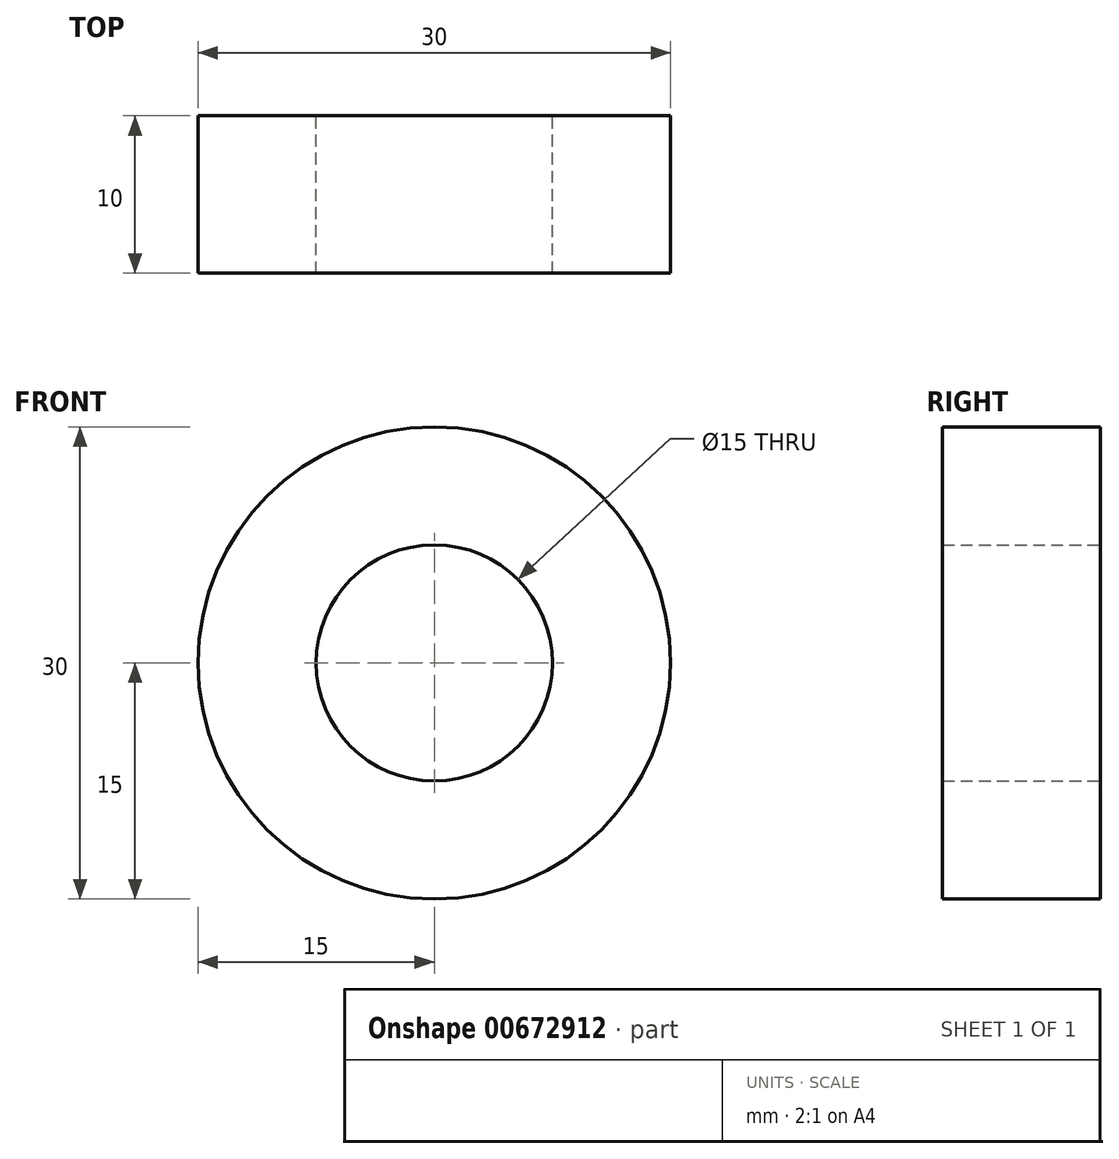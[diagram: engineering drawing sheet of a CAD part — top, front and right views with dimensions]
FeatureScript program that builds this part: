
annotation { "Feature Type Name" : "Feature", "Feature Type Description" : "" }
export const myFeature = defineFeature(function(context is Context, id is Id, definition is map)
    precondition{}
    {
        {
            var Q0;
            Q0=qCreatedBy(makeId("Front.planeOp"),FACE);
            var sketch = newSketch(context, id + "F0", { "sketchPlane" : qUnion([Q0])});
            skCircle(sketch, "E0", {"center": v(0, 0) * mm, "radius": 15 * mm});
            skCircle(sketch, "E1", {"center": v(0, 0) * mm, "radius": 7.5 * mm});
            skSolve(sketch);
        }
        {
            var Q0;
            Q0=makeQuery(id+"F0.imprint","IMPRINT",FACE,{"disambiguationData":[TD([[makeQuery(id+"F0.imprint","IMPRINT",EDGE,{"derivedFrom":sQuery(id+"F0.wireOp",EDGE,"E0")}),1.0]])]});
            extrude(context, id + "F1", {"entities" : qUnion([Q0]), "depth" : 10 * mm, "offsetDistance" : 25 * mm});
        }
    });
